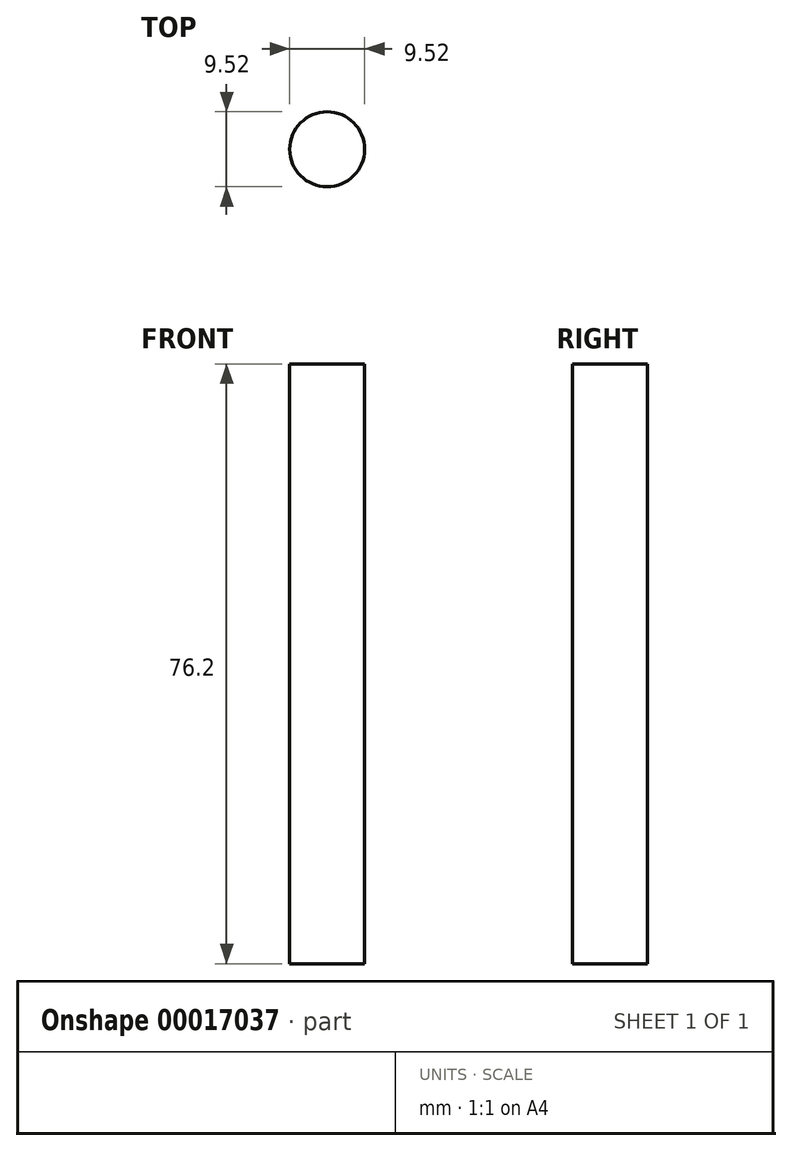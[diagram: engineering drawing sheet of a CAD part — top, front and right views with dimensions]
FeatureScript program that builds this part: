
annotation { "Feature Type Name" : "Feature", "Feature Type Description" : "" }
export const myFeature = defineFeature(function(context is Context, id is Id, definition is map)
    precondition{}
    {
        {
            var Q0;
            Q0=qCreatedBy(makeId("Top.planeOp"),FACE);
            var sketch = newSketch(context, id + "F0", { "sketchPlane" : qUnion([Q0])});
            skCircle(sketch, "E0", {"center": v(0, 0) * mm, "radius": 4.76 * mm});
            skSolve(sketch);
        }
        {
            var Q0;
            Q0=makeQuery(id+"F0.imprint","IMPRINT",FACE,{"disambiguationData":[TD([[makeQuery(id+"F0.imprint","IMPRINT",EDGE,{"derivedFrom":sQuery(id+"F0.wireOp",EDGE,"E0")}),1.0]])]});
            extrude(context, id + "F1", {"entities" : qUnion([Q0]), "depth" : 76.2 * mm});
        }
    });
